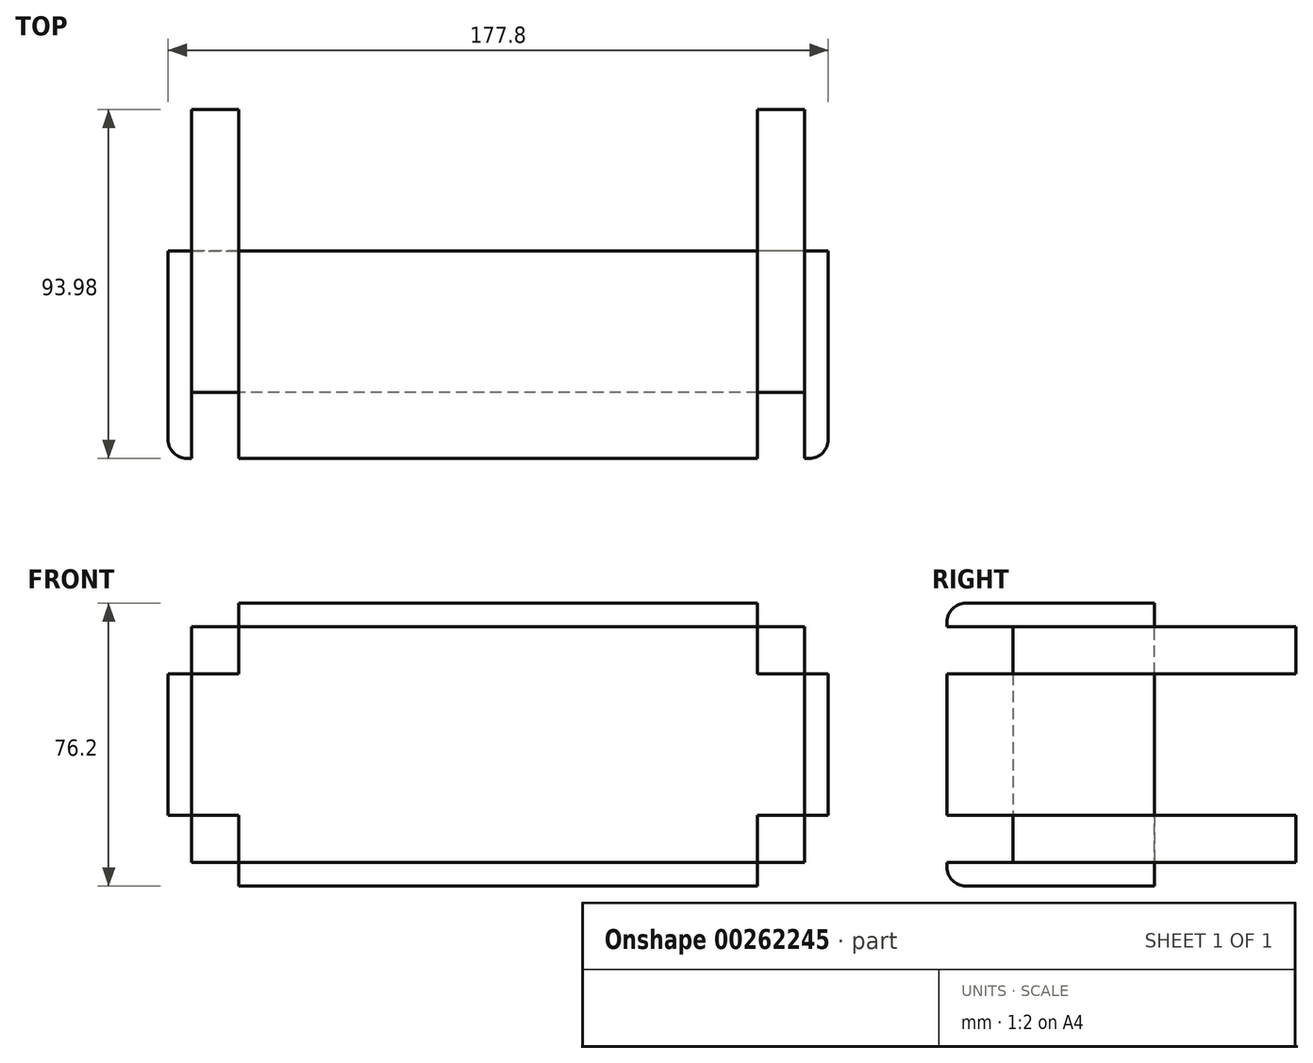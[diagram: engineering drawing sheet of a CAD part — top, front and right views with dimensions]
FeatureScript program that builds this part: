
annotation { "Feature Type Name" : "Feature", "Feature Type Description" : "" }
export const myFeature = defineFeature(function(context is Context, id is Id, definition is map)
    precondition{}
    {
        {
            var Q0;
            Q0=qCreatedBy(makeId("Front.planeOp"),FACE);
            var sketch = newSketch(context, id + "F0", { "sketchPlane" : qUnion([Q0])});
            skLineSegment(sketch, "E0.bottom", {"start": v(88.9, 38.1) * mm, "end": v(-88.9, 38.1) * mm});
            skLineSegment(sketch, "E0.top", {"start": v(88.9, -38.1) * mm, "end": v(-88.9, -38.1) * mm});
            skLineSegment(sketch, "E0.left", {"start": v(88.9, 38.1) * mm, "end": v(88.9, -38.1) * mm});
            skLineSegment(sketch, "E0.right", {"start": v(-88.9, 38.1) * mm, "end": v(-88.9, -38.1) * mm});
            skPoint(sketch, "E0.middle", {"position": v(0, 0) * mm});
            skLineSegment(sketch, "E1.bottom", {"start": v(82.55, 31.75) * mm, "end": v(-82.55, 31.75) * mm});
            skLineSegment(sketch, "E1.top", {"start": v(82.55, -31.75) * mm, "end": v(-82.55, -31.75) * mm});
            skLineSegment(sketch, "E1.left", {"start": v(82.55, 31.75) * mm, "end": v(82.55, -31.75) * mm});
            skLineSegment(sketch, "E1.right", {"start": v(-82.55, 31.75) * mm, "end": v(-82.55, -31.75) * mm});
            skLineSegment(sketch, "E2", {"start": v(-88.9, 38.1) * mm, "end": v(-88.9, 19.05) * mm});
            skLineSegment(sketch, "E3", {"start": v(-88.9, 19.05) * mm, "end": v(-69.85, 19.05) * mm});
            skLineSegment(sketch, "E4", {"start": v(-69.85, 19.05) * mm, "end": v(-69.85, 38.1) * mm});
            skLineSegment(sketch, "E5", {"start": v(-69.85, 38.1) * mm, "end": v(-88.9, 38.1) * mm});
            skLineSegment(sketch, "E6", {"start": v(-88.9, -38.1) * mm, "end": v(-69.85, -38.1) * mm});
            skLineSegment(sketch, "E7", {"start": v(-69.85, -38.1) * mm, "end": v(-69.85, -19.05) * mm});
            skLineSegment(sketch, "E8", {"start": v(-69.85, -19.05) * mm, "end": v(-88.9, -19.05) * mm});
            skLineSegment(sketch, "E9", {"start": v(-88.9, -19.05) * mm, "end": v(-88.9, -38.1) * mm});
            skLineSegment(sketch, "E10", {"start": v(88.9, -38.1) * mm, "end": v(88.9, -19.05) * mm});
            skLineSegment(sketch, "E11", {"start": v(88.9, -19.05) * mm, "end": v(69.85, -19.05) * mm});
            skLineSegment(sketch, "E12", {"start": v(69.85, -19.05) * mm, "end": v(69.85, -38.1) * mm});
            skLineSegment(sketch, "E13", {"start": v(69.85, -38.1) * mm, "end": v(88.9, -38.1) * mm});
            skLineSegment(sketch, "E14", {"start": v(88.9, 38.1) * mm, "end": v(88.9, 19.05) * mm});
            skLineSegment(sketch, "E15", {"start": v(88.9, 19.05) * mm, "end": v(69.85, 19.05) * mm});
            skLineSegment(sketch, "E16", {"start": v(69.85, 19.05) * mm, "end": v(69.85, 38.1) * mm});
            skLineSegment(sketch, "E17", {"start": v(69.85, 38.1) * mm, "end": v(88.9, 38.1) * mm});
            skSolve(sketch);
        }
        {
            var Q0;
            {var subQ1=sQuery(id+"F0.wireOp",EDGE,"E2");Q0=makeQuery(id+"F0.imprint","IMPRINT",FACE,{"disambiguationData":[TD([[makeQuery(id+"F0.imprint","IMPRINT",EDGE,{"derivedFrom":subQ1}),1.0]])]});}
            var Q1;
            {var subQ0=sQuery(id+"F0.wireOp",EDGE,"E0.bottom");Q1=makeQuery(id+"F0.imprint","IMPRINT",FACE,{"disambiguationData":[TD([[makeQuery(id+"F0.imprint","IMPRINT",EDGE,{"derivedFrom":subQ0}),1.0]])]});}
            var Q2;
            {var subQ5=sQuery(id+"F0.wireOp",EDGE,"E14");Q2=makeQuery(id+"F0.imprint","IMPRINT",FACE,{"disambiguationData":[TD([[makeQuery(id+"F0.imprint","IMPRINT",EDGE,{"derivedFrom":subQ5}),-1.0]])]});}
            var Q3;
            {var subQ0=sQuery(id+"F0.wireOp",EDGE,"E0.left");Q3=makeQuery(id+"F0.imprint","IMPRINT",FACE,{"disambiguationData":[TD([[makeQuery(id+"F0.imprint","IMPRINT",EDGE,{"derivedFrom":subQ0}),-1.0]])]});}
            var Q4;
            {var subQ1=sQuery(id+"F0.wireOp",EDGE,"E10");Q4=makeQuery(id+"F0.imprint","IMPRINT",FACE,{"disambiguationData":[TD([[makeQuery(id+"F0.imprint","IMPRINT",EDGE,{"derivedFrom":subQ1}),1.0]])]});}
            var Q5;
            {var subQ0=sQuery(id+"F0.wireOp",EDGE,"E0.top");Q5=makeQuery(id+"F0.imprint","IMPRINT",FACE,{"disambiguationData":[TD([[makeQuery(id+"F0.imprint","IMPRINT",EDGE,{"derivedFrom":subQ0}),-1.0]])]});}
            var Q6;
            {var subQ1=sQuery(id+"F0.wireOp",EDGE,"E6");Q6=makeQuery(id+"F0.imprint","IMPRINT",FACE,{"disambiguationData":[TD([[makeQuery(id+"F0.imprint","IMPRINT",EDGE,{"derivedFrom":subQ1}),1.0]])]});}
            var Q7;
            {var subQ0=sQuery(id+"F0.wireOp",EDGE,"E0.right");Q7=makeQuery(id+"F0.imprint","IMPRINT",FACE,{"disambiguationData":[TD([[makeQuery(id+"F0.imprint","IMPRINT",EDGE,{"derivedFrom":subQ0}),1.0]])]});}
            extrude(context, id + "F1", {"entities" : qUnion([Q0, Q1, Q2, Q3, Q4, Q5, Q6, Q7]), "depth" : 55.88 * mm});
        }
        {
            var Q0;
            {var subQ5=sQuery(id+"F0.wireOp",EDGE,"E16");var subQ8=sQuery(id+"F0.wireOp",EDGE,"E1.bottom");var subQ9=makeQuery(id+"F0.imprint","INTERSECT",VERTEX,{"derivedFrom":[subQ8,subQ5]});Q0=makeQuery(id+"F0.imprint","IMPRINT",FACE,{"disambiguationData":[TD([[makeQuery(id+"F0.imprint","IMPRINT",EDGE,{"disambiguationData":[TD([[subQ9,-1.0]])],"derivedFrom":subQ8}),1.0]])]});}
            extrude(context, id + "F2", {"entities" : qUnion([Q0]), "operationType" : NewBodyOperationType.ADD, "depth" : 38.1 * mm});
        }
        {
            var Q0;
            {var subQ0=sQuery(id+"F0.wireOp",EDGE,"E1.right");var subQ1=sQuery(id+"F0.wireOp",EDGE,"E1.bottom");var subQ2=makeQuery(id+"F0.imprint","INTERSECT",VERTEX,{"derivedFrom":[subQ1,subQ0]});Q0=makeQuery(id+"F0.imprint","IMPRINT",FACE,{"disambiguationData":[TD([[makeQuery(id+"F0.imprint","IMPRINT",EDGE,{"disambiguationData":[TD([[subQ2,1.0]])],"derivedFrom":subQ1}),1.0]])]});}
            var Q1;
            {var subQ0=sQuery(id+"F0.wireOp",EDGE,"E1.right");var subQ1=sQuery(id+"F0.wireOp",EDGE,"E1.top");var subQ2=makeQuery(id+"F0.imprint","INTERSECT",VERTEX,{"derivedFrom":[subQ1,subQ0]});Q1=makeQuery(id+"F0.imprint","IMPRINT",FACE,{"disambiguationData":[TD([[makeQuery(id+"F0.imprint","IMPRINT",EDGE,{"disambiguationData":[TD([[subQ2,1.0]])],"derivedFrom":subQ1}),-1.0]])]});}
            var Q2;
            {var subQ0=sQuery(id+"F0.wireOp",EDGE,"E1.left");var subQ1=sQuery(id+"F0.wireOp",EDGE,"E1.top");var subQ2=makeQuery(id+"F0.imprint","INTERSECT",VERTEX,{"derivedFrom":[subQ1,subQ0]});Q2=makeQuery(id+"F0.imprint","IMPRINT",FACE,{"disambiguationData":[TD([[makeQuery(id+"F0.imprint","IMPRINT",EDGE,{"disambiguationData":[TD([[subQ2,-1.0]])],"derivedFrom":subQ1}),-1.0]])]});}
            var Q3;
            {var subQ0=sQuery(id+"F0.wireOp",EDGE,"E1.left");var subQ1=sQuery(id+"F0.wireOp",EDGE,"E1.bottom");var subQ2=makeQuery(id+"F0.imprint","INTERSECT",VERTEX,{"derivedFrom":[subQ1,subQ0]});Q3=makeQuery(id+"F0.imprint","IMPRINT",FACE,{"disambiguationData":[TD([[makeQuery(id+"F0.imprint","IMPRINT",EDGE,{"disambiguationData":[TD([[subQ2,-1.0]])],"derivedFrom":subQ1}),1.0]])]});}
            extrude(context, id + "F3", {"entities" : qUnion([Q0, Q1, Q2, Q3]), "endBound" : BoundingType.SYMMETRIC, "oppositeDirection" : true, "depth" : 76.2 * mm});
        }
        {
            var Q0;
            Q0=makeQuery(id+"F1.opExtrude","CAP_EDGE",EDGE,{"disambiguationData":[OSD([sQuery(id+"F0.wireOp",EDGE,"E0.right"),sQuery(id+"F0.wireOp",EDGE,"E2"),sQuery(id+"F0.wireOp",EDGE,"E9")])],"isStart":false});
            var Q1;
            Q1=makeQuery(id+"F1.opExtrude","CAP_EDGE",EDGE,{"disambiguationData":[OSD([sQuery(id+"F0.wireOp",EDGE,"E0.bottom"),sQuery(id+"F0.wireOp",EDGE,"E5"),sQuery(id+"F0.wireOp",EDGE,"E17")])],"isStart":false});
            var Q2;
            Q2=makeQuery(id+"F1.opExtrude","CAP_EDGE",EDGE,{"disambiguationData":[OSD([sQuery(id+"F0.wireOp",EDGE,"E0.top"),sQuery(id+"F0.wireOp",EDGE,"E6"),sQuery(id+"F0.wireOp",EDGE,"E13")])],"isStart":false});
            var Q3;
            Q3=makeQuery(id+"F1.opExtrude","CAP_EDGE",EDGE,{"disambiguationData":[OSD([sQuery(id+"F0.wireOp",EDGE,"E0.left"),sQuery(id+"F0.wireOp",EDGE,"E10"),sQuery(id+"F0.wireOp",EDGE,"E14")])],"isStart":false});
            fillet(context, id + "F4", {"entities" : qUnion([Q0, Q1, Q2, Q3]), "radius" : 5.08 * mm, "tangentPropagation" : true, "allowEdgeOverflow" : false});
        }
    });
